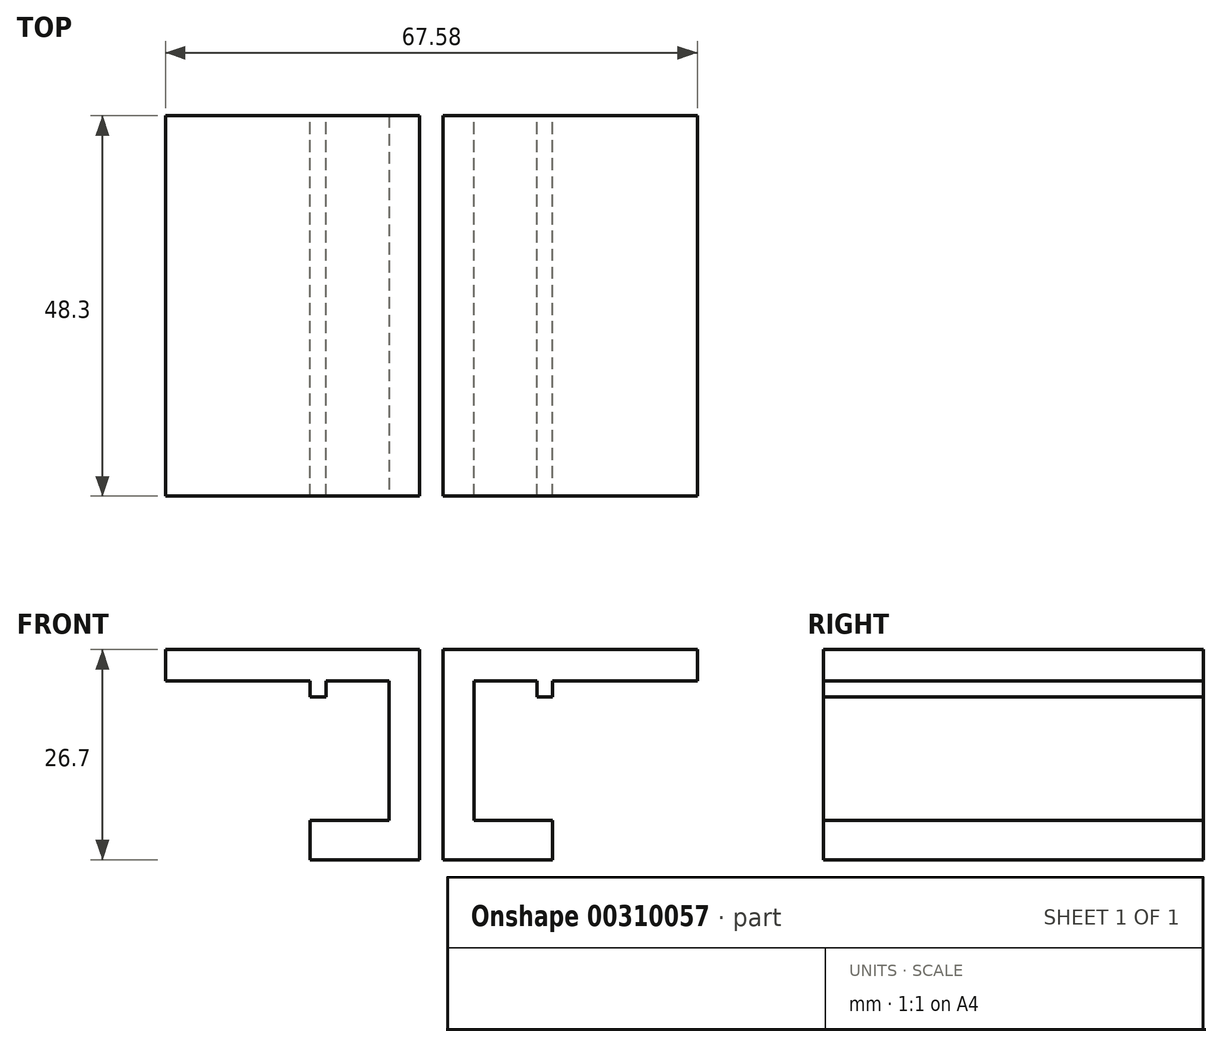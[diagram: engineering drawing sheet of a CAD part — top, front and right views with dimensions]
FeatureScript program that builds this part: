
annotation { "Feature Type Name" : "Feature", "Feature Type Description" : "" }
export const myFeature = defineFeature(function(context is Context, id is Id, definition is map)
    precondition{}
    {
        {
            var Q0;
            Q0=qCreatedBy(makeId("Top.planeOp"),FACE);
            var sketch = newSketch(context, id + "F0", { "sketchPlane" : qUnion([Q0])});
            skLineSegment(sketch, "E0.bottom", {"start": v(15.4, -24.15) * mm, "end": v(-15.4, -24.15) * mm});
            skLineSegment(sketch, "E0.top", {"start": v(15.4, 24.15) * mm, "end": v(-15.4, 24.15) * mm});
            skLineSegment(sketch, "E0.left", {"start": v(15.4, -24.15) * mm, "end": v(15.4, 24.15) * mm});
            skLineSegment(sketch, "E0.right", {"start": v(-15.4, -24.15) * mm, "end": v(-15.4, 24.15) * mm});
            skPoint(sketch, "E0.middle", {"position": v(0, 0) * mm});
            skSolve(sketch);
        }
        {
            var Q0;
            Q0=makeQuery(id+"F0.imprint","IMPRINT",FACE,{"disambiguationData":[TD([[makeQuery(id+"F0.imprint","IMPRINT",EDGE,{"derivedFrom":sQuery(id+"F0.wireOp",EDGE,"E0.bottom")}),-1.0]])]});
            extrude(context, id + "F1", {"entities" : qUnion([Q0]), "oppositeDirection" : true, "depth" : 26.7 * mm});
        }
        {
            var Q0;
            Q0=makeQuery(id+"F1.opExtrude","SWEPT_FACE",FACE,{"disambiguationData":[OSD([sQuery(id+"F0.wireOp",EDGE,"E0.left")])]});
            var sketch = newSketch(context, id + "F2", { "sketchPlane" : qUnion([Q0])});
            skLineSegment(sketch, "E1.bottom", {"start": v(-24.15, 0) * mm, "end": v(24.15, 0) * mm});
            skLineSegment(sketch, "E1.top", {"start": v(-24.15, -21.7) * mm, "end": v(24.15, -21.7) * mm});
            skLineSegment(sketch, "E1.left", {"start": v(-24.15, 0) * mm, "end": v(-24.15, -21.7) * mm});
            skLineSegment(sketch, "E1.right", {"start": v(24.15, 0) * mm, "end": v(24.15, -21.7) * mm});
            skSolve(sketch);
        }
        {
            var Q0;
            Q0=makeQuery(id+"F1.opExtrude","SWEPT_FACE",FACE,{"disambiguationData":[OSD([sQuery(id+"F0.wireOp",EDGE,"E0.right")])]});
            var sketch = newSketch(context, id + "F3", { "sketchPlane" : qUnion([Q0])});
            skLineSegment(sketch, "E2.bottom", {"start": v(-24.15, 0) * mm, "end": v(24.15, 0) * mm});
            skLineSegment(sketch, "E2.top", {"start": v(-24.15, -21.7) * mm, "end": v(24.15, -21.7) * mm});
            skLineSegment(sketch, "E2.left", {"start": v(-24.15, 0) * mm, "end": v(-24.15, -21.7) * mm});
            skLineSegment(sketch, "E2.right", {"start": v(24.15, 0) * mm, "end": v(24.15, -21.7) * mm});
            skSolve(sketch);
        }
        {
            var Q0;
            Q0=makeQuery(id+"F2.imprint","IMPRINT",FACE,{"disambiguationData":[TD([[makeQuery(id+"F2.imprint","IMPRINT",EDGE,{"derivedFrom":sQuery(id+"F2.wireOp",EDGE,"E1.bottom")}),-1.0]])]});
            extrude(context, id + "F4", {"entities" : qUnion([Q0]), "operationType" : NewBodyOperationType.REMOVE, "oppositeDirection" : true, "depth" : 10 * mm});
        }
        {
            var Q0;
            Q0=makeQuery(id+"F3.imprint","IMPRINT",FACE,{"disambiguationData":[TD([[makeQuery(id+"F3.imprint","IMPRINT",EDGE,{"derivedFrom":sQuery(id+"F3.wireOp",EDGE,"E2.bottom")}),1.0]])]});
            extrude(context, id + "F5", {"entities" : qUnion([Q0]), "operationType" : NewBodyOperationType.REMOVE, "oppositeDirection" : true, "depth" : 10 * mm});
        }
        {
            var Q0;
            Q0=makeQuery(id+"F5.boolean.opBoolean","COPY",FACE,{"derivedFrom":makeQuery(id+"F5.opExtrude","CAP_FACE",FACE,{"disambiguationData":[OSD([sQuery(id+"F3.wireOp",EDGE,"E2.bottom"),sQuery(id+"F3.wireOp",EDGE,"E2.top"),sQuery(id+"F3.wireOp",EDGE,"E2.left"),sQuery(id+"F3.wireOp",EDGE,"E2.right")])],"isStart":false})});
            var sketch = newSketch(context, id + "F6", { "sketchPlane" : qUnion([Q0])});
            skLineSegment(sketch, "E3.bottom", {"start": v(-24.15, 0) * mm, "end": v(24.15, 0) * mm});
            skLineSegment(sketch, "E3.top", {"start": v(-24.15, -4) * mm, "end": v(24.15, -4) * mm});
            skLineSegment(sketch, "E3.left", {"start": v(-24.15, 0) * mm, "end": v(-24.15, -4) * mm});
            skLineSegment(sketch, "E3.right", {"start": v(24.15, 0) * mm, "end": v(24.15, -4) * mm});
            skSolve(sketch);
        }
        {
            var Q0;
            Q0=makeQuery(id+"F4.boolean.opBoolean","COPY",FACE,{"derivedFrom":makeQuery(id+"F4.opExtrude","CAP_FACE",FACE,{"disambiguationData":[OSD([sQuery(id+"F2.wireOp",EDGE,"E1.bottom"),sQuery(id+"F2.wireOp",EDGE,"E1.top"),sQuery(id+"F2.wireOp",EDGE,"E1.left"),sQuery(id+"F2.wireOp",EDGE,"E1.right")])],"isStart":false})});
            var sketch = newSketch(context, id + "F7", { "sketchPlane" : qUnion([Q0])});
            skLineSegment(sketch, "E4.bottom", {"start": v(-24.15, 0) * mm, "end": v(24.15, 0) * mm});
            skLineSegment(sketch, "E4.top", {"start": v(-24.15, -4) * mm, "end": v(24.15, -4) * mm});
            skLineSegment(sketch, "E4.left", {"start": v(-24.15, 0) * mm, "end": v(-24.15, -4) * mm});
            skLineSegment(sketch, "E4.right", {"start": v(24.15, 0) * mm, "end": v(24.15, -4) * mm});
            skSolve(sketch);
        }
        {
            var Q0;
            Q0=makeQuery(id+"F7.imprint","IMPRINT",FACE,{"disambiguationData":[TD([[makeQuery(id+"F7.imprint","IMPRINT",EDGE,{"derivedFrom":sQuery(id+"F7.wireOp",EDGE,"E4.bottom")}),-1.0]])]});
            extrude(context, id + "F8", {"entities" : qUnion([Q0]), "operationType" : NewBodyOperationType.ADD, "depth" : 28.4 * mm});
        }
        {
            var Q0;
            Q0=makeQuery(id+"F6.imprint","IMPRINT",FACE,{"disambiguationData":[TD([[makeQuery(id+"F6.imprint","IMPRINT",EDGE,{"derivedFrom":sQuery(id+"F6.wireOp",EDGE,"E3.bottom")}),1.0]])]});
            extrude(context, id + "F9", {"entities" : qUnion([Q0]), "operationType" : NewBodyOperationType.ADD, "depth" : 28.4 * mm});
        }
        {
            var Q0;
            Q0=makeQuery(id+"F8.opExtrude","SWEPT_FACE",FACE,{"disambiguationData":[OSD([sQuery(id+"F7.wireOp",EDGE,"E4.top")])]});
            var sketch = newSketch(context, id + "F10", { "sketchPlane" : qUnion([Q0])});
            skLineSegment(sketch, "E5.bottom", {"start": v(15.4, 24.15) * mm, "end": v(13.4, 24.15) * mm});
            skLineSegment(sketch, "E5.top", {"start": v(15.4, -24.15) * mm, "end": v(13.4, -24.15) * mm});
            skLineSegment(sketch, "E5.left", {"start": v(15.4, 24.15) * mm, "end": v(15.4, -24.15) * mm});
            skLineSegment(sketch, "E5.right", {"start": v(13.4, 24.15) * mm, "end": v(13.4, -24.15) * mm});
            skSolve(sketch);
        }
        {
            var Q0;
            Q0=makeQuery(id+"F10.imprint","IMPRINT",FACE,{"disambiguationData":[TD([[makeQuery(id+"F10.imprint","IMPRINT",EDGE,{"derivedFrom":sQuery(id+"F10.wireOp",EDGE,"E5.bottom")}),1.0]])]});
            extrude(context, id + "F11", {"entities" : qUnion([Q0]), "operationType" : NewBodyOperationType.ADD, "depth" : 2 * mm});
        }
        {
            var Q0;
            Q0=makeQuery(id+"F9.opExtrude","SWEPT_FACE",FACE,{"disambiguationData":[OSD([sQuery(id+"F6.wireOp",EDGE,"E3.top")])]});
            var sketch = newSketch(context, id + "F12", { "sketchPlane" : qUnion([Q0])});
            skLineSegment(sketch, "E6.bottom", {"start": v(-15.4, 24.15) * mm, "end": v(-13.4, 24.15) * mm});
            skLineSegment(sketch, "E6.top", {"start": v(-15.4, -24.15) * mm, "end": v(-13.4, -24.15) * mm});
            skLineSegment(sketch, "E6.left", {"start": v(-15.4, 24.15) * mm, "end": v(-15.4, -24.15) * mm});
            skLineSegment(sketch, "E6.right", {"start": v(-13.4, 24.15) * mm, "end": v(-13.4, -24.15) * mm});
            skSolve(sketch);
        }
        {
            var Q0;
            Q0=makeQuery(id+"F12.imprint","IMPRINT",FACE,{"disambiguationData":[TD([[makeQuery(id+"F12.imprint","IMPRINT",EDGE,{"derivedFrom":sQuery(id+"F12.wireOp",EDGE,"E6.bottom")}),-1.0]])]});
            extrude(context, id + "F13", {"entities" : qUnion([Q0]), "operationType" : NewBodyOperationType.ADD, "depth" : 2 * mm});
        }
        {
            var Q0;
            Q0=makeQuery(id+"F9.boolean.opBoolean","MERGE",FACE,{"derivedFrom":[makeQuery(id+"F8.boolean.opBoolean","MERGE",FACE,{"derivedFrom":[makeQuery(id+"F1.opExtrude","CAP_FACE",FACE,{"disambiguationData":[OSD([sQuery(id+"F0.wireOp",EDGE,"E0.bottom"),sQuery(id+"F0.wireOp",EDGE,"E0.top"),sQuery(id+"F0.wireOp",EDGE,"E0.left"),sQuery(id+"F0.wireOp",EDGE,"E0.right")])],"isStart":true}),makeQuery(id+"F8.opExtrude","SWEPT_FACE",FACE,{"disambiguationData":[OSD([sQuery(id+"F7.wireOp",EDGE,"E4.bottom")])]})]}),makeQuery(id+"F9.opExtrude","SWEPT_FACE",FACE,{"disambiguationData":[OSD([sQuery(id+"F6.wireOp",EDGE,"E3.bottom")])]})]});
            var sketch = newSketch(context, id + "F14", { "sketchPlane" : qUnion([Q0])});
            skLineSegment(sketch, "E7.bottom", {"start": v(0, -24.15) * mm, "end": v(0, -24.15) * mm});
            skLineSegment(sketch, "E7.top", {"start": v(0, 24.15) * mm, "end": v(0, 24.15) * mm});
            skLineSegment(sketch, "E7.left", {"start": v(0, -24.15) * mm, "end": v(0, 24.15) * mm});
            skLineSegment(sketch, "E7.right", {"start": v(0, -24.15) * mm, "end": v(0, 24.15) * mm});
            skPoint(sketch, "E7.middle", {"position": v(0, 0) * mm});
            skSolve(sketch);
        }
        {
            var Q0;
            Q0=makeQuery(id+"F14.imprint","IMPRINT",FACE,{"disambiguationData":[TD([[makeQuery(id+"F14.imprint","IMPRINT",EDGE,{"derivedFrom":sQuery(id+"F14.wireOp",EDGE,"E7.bottom")}),-1.0]])]});
            extrude(context, id + "F15", {"entities" : qUnion([Q0]), "operationType" : NewBodyOperationType.REMOVE, "endBound" : BoundingType.UP_TO_NEXT, "oppositeDirection" : true, "depth" : 25 * mm});
        }
        {
            var Q0;
            Q0=makeQuery(id+"F15.boolean.opBoolean","COPY",FACE,{"derivedFrom":makeQuery(id+"F15.opExtrude","SWEPT_FACE",FACE,{"disambiguationData":[OSD([sQuery(id+"F14.wireOp",EDGE,"E7.left")])]})});
            extrude(context, id + "F16", {"entities" : qUnion([Q0]), "operationType" : NewBodyOperationType.REMOVE, "oppositeDirection" : true, "depth" : 1.5 * mm});
        }
        {
            var Q0;
            Q0=makeQuery(id+"F15.boolean.opBoolean","COPY",FACE,{"derivedFrom":makeQuery(id+"F15.opExtrude","SWEPT_FACE",FACE,{"disambiguationData":[OSD([sQuery(id+"F14.wireOp",EDGE,"E7.right")])]})});
            extrude(context, id + "F17", {"entities" : qUnion([Q0]), "operationType" : NewBodyOperationType.REMOVE, "oppositeDirection" : true, "depth" : 1.5 * mm});
        }
    });
